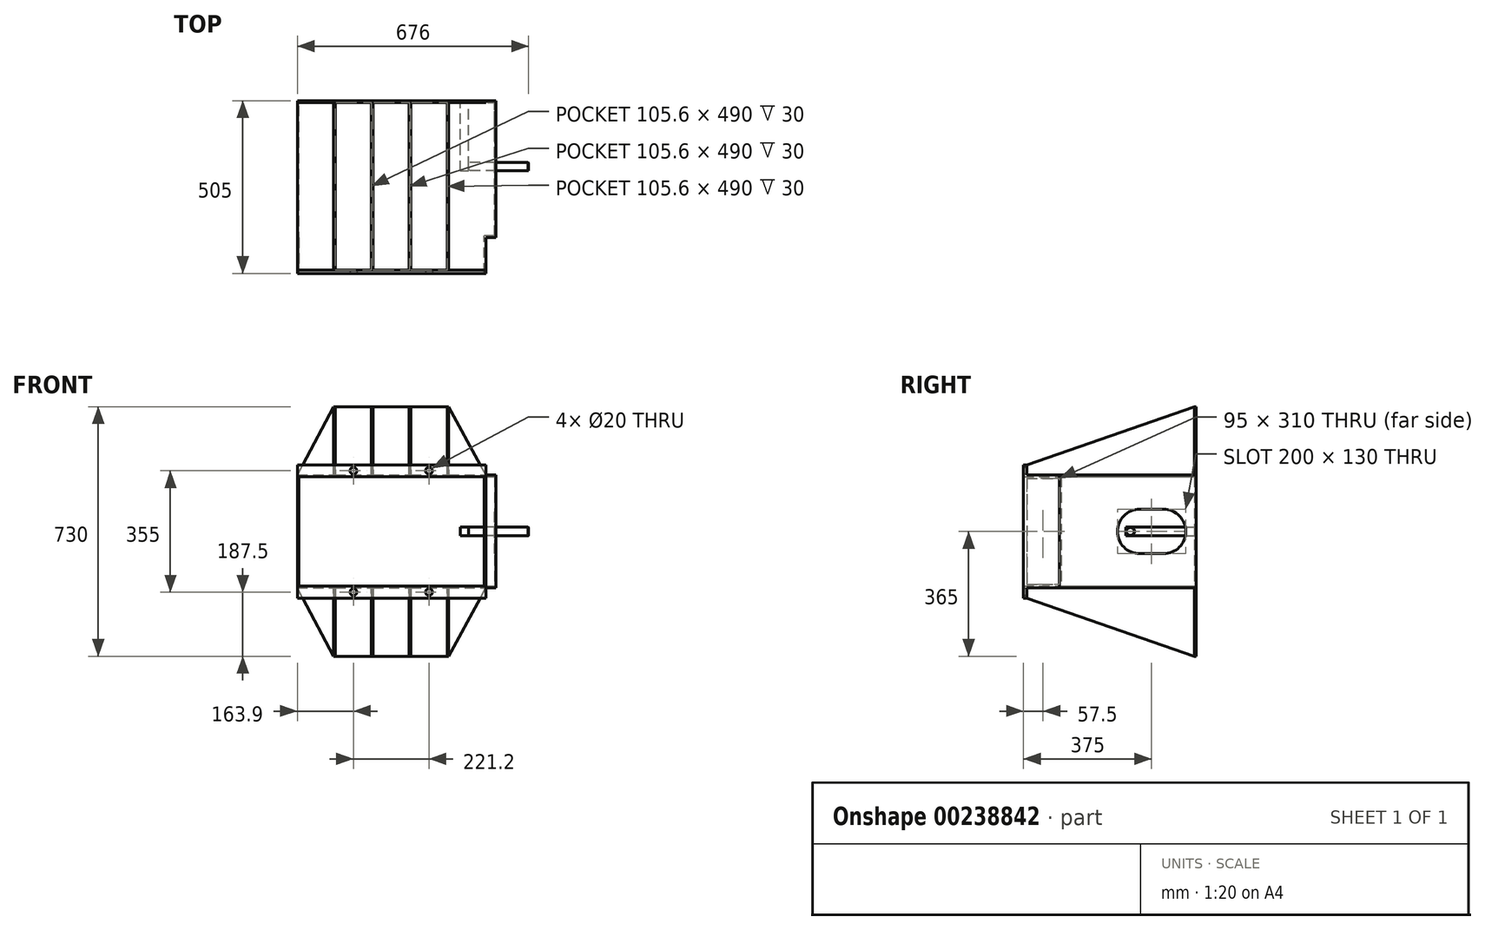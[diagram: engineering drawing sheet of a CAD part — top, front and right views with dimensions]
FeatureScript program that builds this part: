
annotation { "Feature Type Name" : "Feature", "Feature Type Description" : "" }
export const myFeature = defineFeature(function(context is Context, id is Id, definition is map)
    precondition{}
    {
        {
            var Q0;
            Q0=qCreatedBy(makeId("Front.planeOp"),FACE);
            var sketch = newSketch(context, id + "F0", { "sketchPlane" : qUnion([Q0])});
            skLineSegment(sketch, "E0.bottom", {"start": v(-376.5, 365) * mm, "end": v(376.5, 365) * mm});
            skLineSegment(sketch, "E0.top", {"start": v(-376.5, -365) * mm, "end": v(376.5, -365) * mm});
            skLineSegment(sketch, "E0.left", {"start": v(-376.5, 365) * mm, "end": v(-376.5, -365) * mm});
            skLineSegment(sketch, "E0.right", {"start": v(376.5, 365) * mm, "end": v(376.5, -365) * mm});
            skSolve(sketch);
        }
        {
            var Q0;
            Q0=makeQuery(id+"F0.imprint","IMPRINT",FACE,{"disambiguationData":[TD([[makeQuery(id+"F0.imprint","IMPRINT",EDGE,{"derivedFrom":sQuery(id+"F0.wireOp",EDGE,"E0.bottom")}),-1.0]])]});
            extrude(context, id + "F1", {"entities" : qUnion([Q0]), "depth" : 5 * mm});
        }
        {
            var Q0;
            Q0=makeQuery(id+"F1.opExtrude","CAP_FACE",FACE,{"disambiguationData":[OSD([sQuery(id+"F0.wireOp",EDGE,"E0.bottom"),sQuery(id+"F0.wireOp",EDGE,"E0.top"),sQuery(id+"F0.wireOp",EDGE,"E0.left"),sQuery(id+"F0.wireOp",EDGE,"E0.right")])],"isStart":false});
            var sketch = newSketch(context, id + "F2", { "sketchPlane" : qUnion([Q0])});
            skLineSegment(sketch, "E1.bottom", {"start": v(-276, 165) * mm, "end": v(275, 165) * mm});
            skLineSegment(sketch, "E1.top", {"start": v(-276, -165) * mm, "end": v(275, -165) * mm});
            skLineSegment(sketch, "E1.left", {"start": v(-276, 165) * mm, "end": v(-276, -165) * mm});
            skLineSegment(sketch, "E1.right", {"start": v(275, 165) * mm, "end": v(275, -165) * mm});
            skLineSegment(sketch, "E2.bottom", {"start": v(-272, 160) * mm, "end": v(271, 160) * mm});
            skLineSegment(sketch, "E2.top", {"start": v(-272, -160) * mm, "end": v(271, -160) * mm});
            skLineSegment(sketch, "E2.left", {"start": v(-272, 160) * mm, "end": v(-272, -160) * mm});
            skLineSegment(sketch, "E2.right", {"start": v(271, 160) * mm, "end": v(271, -160) * mm});
            skSolve(sketch);
        }
        {
            var Q0;
            Q0=makeQuery(id+"F2.imprint","IMPRINT",FACE,{"disambiguationData":[TD([[makeQuery(id+"F2.imprint","IMPRINT",EDGE,{"derivedFrom":sQuery(id+"F2.wireOp",EDGE,"E1.bottom")}),-1.0]])]});
            extrude(context, id + "F3", {"entities" : qUnion([Q0]), "operationType" : NewBodyOperationType.ADD, "depth" : 500 * mm});
        }
        {
            var Q0;
            Q0=makeQuery(id+"F3.opExtrude","SWEPT_FACE",FACE,{"disambiguationData":[OSD([sQuery(id+"F2.wireOp",EDGE,"E1.left")])]});
            var sketch = newSketch(context, id + "F4", { "sketchPlane" : qUnion([Q0])});
            skLineSegment(sketch, "E3.bottom", {"start": v(505, 165) * mm, "end": v(495, 165) * mm});
            skLineSegment(sketch, "E3.top", {"start": v(505, 195) * mm, "end": v(495, 195) * mm});
            skLineSegment(sketch, "E3.left", {"start": v(505, 165) * mm, "end": v(505, 195) * mm});
            skLineSegment(sketch, "E3.right", {"start": v(495, 165) * mm, "end": v(495, 195) * mm});
            skLineSegment(sketch, "E4.bottom", {"start": v(505, -165) * mm, "end": v(495, -165) * mm});
            skLineSegment(sketch, "E4.top", {"start": v(505, -195) * mm, "end": v(495, -195) * mm});
            skLineSegment(sketch, "E4.left", {"start": v(505, -165) * mm, "end": v(505, -195) * mm});
            skLineSegment(sketch, "E4.right", {"start": v(495, -165) * mm, "end": v(495, -195) * mm});
            skSolve(sketch);
        }
        {
            var Q0;
            Q0=makeQuery(id+"F4.imprint","IMPRINT",FACE,{"disambiguationData":[TD([[makeQuery(id+"F4.imprint","IMPRINT",EDGE,{"derivedFrom":sQuery(id+"F4.wireOp",EDGE,"E3.bottom")}),-1.0]])]});
            var Q1;
            Q1=makeQuery(id+"F4.imprint","IMPRINT",FACE,{"disambiguationData":[TD([[makeQuery(id+"F4.imprint","IMPRINT",EDGE,{"derivedFrom":sQuery(id+"F4.wireOp",EDGE,"E4.bottom")}),1.0]])]});
            var Q2;
            Q2=makeQuery(id+"F3.opExtrude","SWEPT_FACE",FACE,{"disambiguationData":[OSD([sQuery(id+"F2.wireOp",EDGE,"E1.right")])]});
            extrude(context, id + "F5", {"entities" : qUnion([Q0, Q1]), "operationType" : NewBodyOperationType.ADD, "endBound" : BoundingType.UP_TO_SURFACE, "oppositeDirection" : true, "endBoundEntityFace" : qUnion([Q2]), "depth" : 25 * mm});
        }
        {
            var Q0;
            {var subQ0=sQuery(id+"F0.wireOp",EDGE,"E0.right");var subQ1=sQuery(id+"F0.wireOp",EDGE,"E0.left");var subQ2=sQuery(id+"F0.wireOp",EDGE,"E0.top");var subQ3=sQuery(id+"F0.wireOp",EDGE,"E0.bottom");Q0=makeQuery(id+"F3.boolean.opBoolean","SPLIT",FACE,{"disambiguationData":[TD([makeQuery(id+"F1.opExtrude","SWEPT_FACE",FACE,{"disambiguationData":[OSD([subQ3])]})])],"derivedFrom":makeQuery(id+"F1.opExtrude","CAP_FACE",FACE,{"disambiguationData":[OSD([subQ3,subQ2,subQ1,subQ0])],"isStart":false})});}
            var sketch = newSketch(context, id + "F6", { "sketchPlane" : qUnion([Q0])});
            skLineSegment(sketch, "E5.bottom", {"start": v(166.9, 365) * mm, "end": v(161.9, 365) * mm});
            skLineSegment(sketch, "E5.top", {"start": v(166.9, 165) * mm, "end": v(161.9, 165) * mm});
            skLineSegment(sketch, "E5.left", {"start": v(166.9, 365) * mm, "end": v(166.9, 165) * mm});
            skLineSegment(sketch, "E5.right", {"start": v(161.9, 365) * mm, "end": v(161.9, 165) * mm});
            skLineSegment(sketch, "E6.bottom", {"start": v(56.3, 365) * mm, "end": v(51.3, 365) * mm});
            skLineSegment(sketch, "E6.top", {"start": v(56.3, 165) * mm, "end": v(51.3, 165) * mm});
            skLineSegment(sketch, "E6.left", {"start": v(56.3, 365) * mm, "end": v(56.3, 165) * mm});
            skLineSegment(sketch, "E6.right", {"start": v(51.3, 365) * mm, "end": v(51.3, 165) * mm});
            skLineSegment(sketch, "E7.bottom", {"start": v(-54.3, 365) * mm, "end": v(-59.3, 365) * mm});
            skLineSegment(sketch, "E7.top", {"start": v(-54.3, 165) * mm, "end": v(-59.3, 165) * mm});
            skLineSegment(sketch, "E7.left", {"start": v(-59.3, 365) * mm, "end": v(-59.3, 165) * mm});
            skLineSegment(sketch, "E7.right", {"start": v(-54.3, 365) * mm, "end": v(-54.3, 165) * mm});
            skLineSegment(sketch, "E8.bottom", {"start": v(-164.9, 365) * mm, "end": v(-169.9, 365) * mm});
            skLineSegment(sketch, "E8.top", {"start": v(-164.9, 165) * mm, "end": v(-169.9, 165) * mm});
            skLineSegment(sketch, "E8.left", {"start": v(-169.9, 365) * mm, "end": v(-169.9, 165) * mm});
            skLineSegment(sketch, "E8.right", {"start": v(-164.9, 365) * mm, "end": v(-164.9, 165) * mm});
            skPoint(sketch, "E9.oppositeSnap0", {"position": v(161.9, 265) * mm});
            skLineSegment(sketch, "E9.bottom", {"start": v(166.9, -365) * mm, "end": v(161.9, -365) * mm});
            skLineSegment(sketch, "E9.top", {"start": v(166.9, -165) * mm, "end": v(161.9, -165) * mm});
            skLineSegment(sketch, "E9.left", {"start": v(166.9, -365) * mm, "end": v(166.9, -165) * mm});
            skLineSegment(sketch, "E9.right", {"start": v(161.9, -365) * mm, "end": v(161.9, -165) * mm});
            skPoint(sketch, "E10.firstSnap0", {"position": v(56.3, 265) * mm});
            skLineSegment(sketch, "E10.bottom", {"start": v(56.3, -365) * mm, "end": v(51.3, -365) * mm});
            skLineSegment(sketch, "E10.top", {"start": v(56.3, -165) * mm, "end": v(51.3, -165) * mm});
            skLineSegment(sketch, "E10.left", {"start": v(56.3, -365) * mm, "end": v(56.3, -165) * mm});
            skLineSegment(sketch, "E10.right", {"start": v(51.3, -365) * mm, "end": v(51.3, -165) * mm});
            skLineSegment(sketch, "E11.bottom", {"start": v(-54.3, -365) * mm, "end": v(-59.3, -365) * mm});
            skLineSegment(sketch, "E11.top", {"start": v(-54.3, -165) * mm, "end": v(-59.3, -165) * mm});
            skLineSegment(sketch, "E11.left", {"start": v(-54.3, -365) * mm, "end": v(-54.3, -165) * mm});
            skLineSegment(sketch, "E11.right", {"start": v(-59.3, -365) * mm, "end": v(-59.3, -165) * mm});
            skPoint(sketch, "E12.oppositeSnap0", {"position": v(-169.9, 265) * mm});
            skLineSegment(sketch, "E12.bottom", {"start": v(-164.9, -365) * mm, "end": v(-169.9, -365) * mm});
            skLineSegment(sketch, "E12.top", {"start": v(-164.9, -165) * mm, "end": v(-169.9, -165) * mm});
            skLineSegment(sketch, "E12.left", {"start": v(-164.9, -365) * mm, "end": v(-164.9, -165) * mm});
            skLineSegment(sketch, "E12.right", {"start": v(-169.9, -365) * mm, "end": v(-169.9, -165) * mm});
            skSolve(sketch);
        }
        {
            var Q0;
            Q0 = qSketchRegion(id + "F6", true);
            var Q1;
            Q1=makeQuery(id+"F5.opExtrude","SWEPT_FACE",FACE,{"disambiguationData":[OSD([sQuery(id+"F4.wireOp",EDGE,"E4.right")])]});
            extrude(context, id + "F7", {"entities" : qUnion([Q0]), "operationType" : NewBodyOperationType.ADD, "endBound" : BoundingType.UP_TO_SURFACE, "endBoundEntityFace" : qUnion([Q1]), "depth" : 25 * mm});
        }
        {
            var Q0;
            Q0=makeQuery(id+"F7.opExtrude","SWEPT_FACE",FACE,{"disambiguationData":[OSD([sQuery(id+"F6.wireOp",EDGE,"E8.left")])]});
            var sketch = newSketch(context, id + "F8", { "sketchPlane" : qUnion([Q0])});
            skLineSegment(sketch, "E13", {"start": v(495, 195) * mm, "end": v(5, 365) * mm});
            skLineSegment(sketch, "E14", {"start": v(5, 365) * mm, "end": v(495, 365) * mm});
            skLineSegment(sketch, "E15", {"start": v(495, 365) * mm, "end": v(495, 195) * mm});
            skSolve(sketch);
        }
        {
            var Q0;
            Q0=makeQuery(id+"F7.opExtrude","SWEPT_FACE",FACE,{"disambiguationData":[OSD([sQuery(id+"F6.wireOp",EDGE,"E12.right")])]});
            var sketch = newSketch(context, id + "F9", { "sketchPlane" : qUnion([Q0])});
            skLineSegment(sketch, "E16", {"start": v(495, -195) * mm, "end": v(5, -365) * mm});
            skLineSegment(sketch, "E17", {"start": v(495, -195) * mm, "end": v(495, -365) * mm});
            skLineSegment(sketch, "E18", {"start": v(495, -365) * mm, "end": v(5, -365) * mm});
            skSolve(sketch);
        }
        {
            var Q0;
            Q0=makeQuery(id+"F8.imprint","IMPRINT",FACE,{"disambiguationData":[TD([[makeQuery(id+"F8.imprint","IMPRINT",EDGE,{"derivedFrom":sQuery(id+"F8.wireOp",EDGE,"E13")}),-1.0]])]});
            var Q1;
            Q1=makeQuery(id+"F9.imprint","IMPRINT",FACE,{"disambiguationData":[TD([[makeQuery(id+"F9.imprint","IMPRINT",EDGE,{"derivedFrom":sQuery(id+"F9.wireOp",EDGE,"E16")}),1.0]])]});
            extrude(context, id + "F10", {"entities" : qUnion([Q0, Q1]), "operationType" : NewBodyOperationType.REMOVE, "endBound" : BoundingType.THROUGH_ALL, "oppositeDirection" : true, "depth" : 25 * mm});
        }
        {
            var Q0;
            {var subQ1=sQuery(id+"F0.wireOp",EDGE,"E0.right");var subQ2=makeQuery(id+"F1.opExtrude","SWEPT_FACE",FACE,{"disambiguationData":[OSD([subQ1])]});var subQ5=sQuery(id+"F0.wireOp",EDGE,"E0.bottom");var subQ6=makeQuery(id+"F1.opExtrude","SWEPT_FACE",FACE,{"disambiguationData":[OSD([subQ5])]});var subQ8=sQuery(id+"F0.wireOp",EDGE,"E0.top");var subQ10=sQuery(id+"F0.wireOp",EDGE,"E0.left");Q0=makeQuery(id+"F7.boolean.opBoolean","SPLIT",FACE,{"disambiguationData":[TD([subQ2])],"derivedFrom":makeQuery(id+"F3.boolean.opBoolean","SPLIT",FACE,{"disambiguationData":[TD([subQ6])],"derivedFrom":makeQuery(id+"F1.opExtrude","CAP_FACE",FACE,{"disambiguationData":[OSD([subQ5,subQ8,subQ10,subQ1])],"isStart":false})})});}
            var sketch = newSketch(context, id + "F11", { "sketchPlane" : qUnion([Q0])});
            skLineSegment(sketch, "E19", {"start": v(166.9, -365) * mm, "end": v(275, -165) * mm});
            skLineSegment(sketch, "E20", {"start": v(275, -165) * mm, "end": v(275, 165) * mm});
            skLineSegment(sketch, "E21", {"start": v(275, 165) * mm, "end": v(166.9, 365) * mm});
            skLineSegment(sketch, "E22", {"start": v(166.9, 365) * mm, "end": v(376.5, 365) * mm});
            skLineSegment(sketch, "E23", {"start": v(376.5, 365) * mm, "end": v(376.5, -365) * mm});
            skLineSegment(sketch, "E24", {"start": v(376.5, -365) * mm, "end": v(166.9, -365) * mm});
            skSolve(sketch);
        }
        {
            var Q0;
            {var subQ1=sQuery(id+"F0.wireOp",EDGE,"E0.left");var subQ2=makeQuery(id+"F1.opExtrude","SWEPT_FACE",FACE,{"disambiguationData":[OSD([subQ1])]});var subQ4=sQuery(id+"F0.wireOp",EDGE,"E0.bottom");var subQ5=makeQuery(id+"F1.opExtrude","SWEPT_FACE",FACE,{"disambiguationData":[OSD([subQ4])]});var subQ7=sQuery(id+"F0.wireOp",EDGE,"E0.top");var subQ9=sQuery(id+"F0.wireOp",EDGE,"E0.right");Q0=makeQuery(id+"F7.boolean.opBoolean","SPLIT",FACE,{"disambiguationData":[TD([subQ2])],"derivedFrom":makeQuery(id+"F3.boolean.opBoolean","SPLIT",FACE,{"disambiguationData":[TD([subQ5])],"derivedFrom":makeQuery(id+"F1.opExtrude","CAP_FACE",FACE,{"disambiguationData":[OSD([subQ4,subQ7,subQ1,subQ9])],"isStart":false})})});}
            var sketch = newSketch(context, id + "F12", { "sketchPlane" : qUnion([Q0])});
            skLineSegment(sketch, "E25", {"start": v(-169.9, -365) * mm, "end": v(-276, -165) * mm});
            skLineSegment(sketch, "E26", {"start": v(-276, -165) * mm, "end": v(-276, 165) * mm});
            skLineSegment(sketch, "E27", {"start": v(-276, 165) * mm, "end": v(-169.9, 365) * mm});
            skLineSegment(sketch, "E28", {"start": v(-169.9, 365) * mm, "end": v(-376.5, 365) * mm});
            skLineSegment(sketch, "E29", {"start": v(-376.5, 365) * mm, "end": v(-376.5, -365) * mm});
            skLineSegment(sketch, "E30", {"start": v(-376.5, -365) * mm, "end": v(-169.9, -365) * mm});
            skSolve(sketch);
        }
        {
            var Q0;
            Q0=makeQuery(id+"F11.imprint","IMPRINT",FACE,{"disambiguationData":[TD([[makeQuery(id+"F11.imprint","IMPRINT",EDGE,{"derivedFrom":sQuery(id+"F11.wireOp",EDGE,"E19")}),-1.0]])]});
            var Q1;
            Q1=makeQuery(id+"F12.imprint","IMPRINT",FACE,{"disambiguationData":[TD([[makeQuery(id+"F12.imprint","IMPRINT",EDGE,{"derivedFrom":sQuery(id+"F12.wireOp",EDGE,"E25")}),1.0]])]});
            extrude(context, id + "F13", {"entities" : qUnion([Q0, Q1]), "operationType" : NewBodyOperationType.REMOVE, "endBound" : BoundingType.THROUGH_ALL, "oppositeDirection" : true, "depth" : 25 * mm});
        }
        {
            var Q0;
            {var subQ0=sQuery(id+"F2.wireOp",EDGE,"E1.right");Q0=makeQuery(id+"F13.boolean.opBoolean","MERGE",FACE,{"derivedFrom":[makeQuery(id+"F5.boolean.opBoolean","MERGE",FACE,{"derivedFrom":[makeQuery(id+"F3.opExtrude","SWEPT_FACE",FACE,{"disambiguationData":[OSD([subQ0])]}),makeQuery(id+"F5.opExtrude","CAP_FACE",FACE,{"disambiguationData":[OSD([subQ0]),ownerDisambiguation([makeQuery(id+"F5.opExtrude","SWEPT_BODY",BODY,{"disambiguationData":[OSD([sQuery(id+"F4.wireOp",EDGE,"E3.bottom"),sQuery(id+"F4.wireOp",EDGE,"E3.top"),sQuery(id+"F4.wireOp",EDGE,"E3.left"),sQuery(id+"F4.wireOp",EDGE,"E3.right")])]})])],"isStart":false}),makeQuery(id+"F5.opExtrude","CAP_FACE",FACE,{"disambiguationData":[OSD([subQ0]),ownerDisambiguation([makeQuery(id+"F5.opExtrude","SWEPT_BODY",BODY,{"disambiguationData":[OSD([sQuery(id+"F4.wireOp",EDGE,"E4.bottom"),sQuery(id+"F4.wireOp",EDGE,"E4.top"),sQuery(id+"F4.wireOp",EDGE,"E4.left"),sQuery(id+"F4.wireOp",EDGE,"E4.right")])]})])],"isStart":false})]}),makeQuery(id+"F13.opExtrude","SWEPT_FACE",FACE,{"disambiguationData":[OSD([sQuery(id+"F11.wireOp",EDGE,"E20")])]})]});}
            var sketch = newSketch(context, id + "F14", { "sketchPlane" : qUnion([Q0])});
            skLineSegment(sketch, "E31.bottom", {"start": v(0, -165) * mm, "end": v(-400, -165) * mm});
            skLineSegment(sketch, "E31.top", {"start": v(0, 165) * mm, "end": v(-400, 165) * mm});
            skLineSegment(sketch, "E31.left", {"start": v(0, -165) * mm, "end": v(0, 165) * mm});
            skLineSegment(sketch, "E31.right", {"start": v(-400, -165) * mm, "end": v(-400, 165) * mm});
            skSolve(sketch);
        }
        {
            var Q0;
            {var subQ2=sQuery(id+"F14.wireOp",EDGE,"E31.left");Q0=makeQuery(id+"F14.imprint","IMPRINT",FACE,{"disambiguationData":[TD([[makeQuery(id+"F14.imprint","IMPRINT",EDGE,{"derivedFrom":subQ2}),-1.0]])]});}
            extrude(context, id + "F15", {"entities" : qUnion([Q0]), "operationType" : NewBodyOperationType.ADD, "depth" : 30 * mm});
        }
        {
            var Q0;
            Q0=makeQuery(id+"F3.opExtrude","SWEPT_FACE",FACE,{"disambiguationData":[OSD([sQuery(id+"F2.wireOp",EDGE,"E2.right")])]});
            var sketch = newSketch(context, id + "F16", { "sketchPlane" : qUnion([Q0])});
            skLineSegment(sketch, "E32.bottom", {"start": v(5, 160) * mm, "end": v(395, 160) * mm});
            skLineSegment(sketch, "E32.top", {"start": v(5, -160) * mm, "end": v(395, -160) * mm});
            skLineSegment(sketch, "E32.left", {"start": v(5, 160) * mm, "end": v(5, -160) * mm});
            skLineSegment(sketch, "E32.right", {"start": v(395, 160) * mm, "end": v(395, -160) * mm});
            skSolve(sketch);
        }
        {
            var Q0;
            Q0=makeQuery(id+"F16.imprint","IMPRINT",FACE,{"disambiguationData":[TD([[makeQuery(id+"F16.imprint","IMPRINT",EDGE,{"derivedFrom":sQuery(id+"F16.wireOp",EDGE,"E32.bottom")}),1.0]])]});
            extrude(context, id + "F17", {"entities" : qUnion([Q0]), "operationType" : NewBodyOperationType.REMOVE, "oppositeDirection" : true, "depth" : 30 * mm});
        }
        {
            var Q0;
            Q0=makeQuery(id+"F15.opExtrude","CAP_FACE",FACE,{"disambiguationData":[OSD([sQuery(id+"F14.wireOp",EDGE,"E31.bottom"),sQuery(id+"F14.wireOp",EDGE,"E31.top"),sQuery(id+"F14.wireOp",EDGE,"E31.left"),sQuery(id+"F14.wireOp",EDGE,"E31.right")])],"isStart":false});
            var sketch = newSketch(context, id + "F18", { "sketchPlane" : qUnion([Q0])});
            skLineSegment(sketch, "E33.bottom", {"start": v(-165, -65) * mm, "end": v(-95, -65) * mm});
            skLineSegment(sketch, "E33.top", {"start": v(-165, 65) * mm, "end": v(-95, 65) * mm});
            skLineSegment(sketch, "E33.left", {"start": v(-165, -65) * mm, "end": v(-165, 65) * mm});
            skLineSegment(sketch, "E33.right", {"start": v(-95, -65) * mm, "end": v(-95, 65) * mm});
            skArc(sketch, "E34", {"start": v(-165, 65) * mm, "mid": v(-230, 0) * mm, "end": v(-165, -65) * mm});
            skArc(sketch, "E35", {"start": v(-95, -65) * mm, "mid": v(-30, 0) * mm, "end": v(-95, 65) * mm});
            skLineSegment(sketch, "E36", {"start": v(-165, 0) * mm, "end": v(-95, 0) * mm, "construction": true});
            skSolve(sketch);
        }
        {
            var Q0;
            Q0=makeQuery(id+"F18.imprint","IMPRINT",FACE,{"disambiguationData":[TD([[makeQuery(id+"F18.imprint","IMPRINT",EDGE,{"derivedFrom":sQuery(id+"F18.wireOp",EDGE,"E33.left")}),1.0]])]});
            var Q1;
            Q1=makeQuery(id+"F18.imprint","IMPRINT",FACE,{"disambiguationData":[TD([[makeQuery(id+"F18.imprint","IMPRINT",EDGE,{"derivedFrom":sQuery(id+"F18.wireOp",EDGE,"E33.bottom")}),1.0]])]});
            var Q2;
            Q2=makeQuery(id+"F18.imprint","IMPRINT",FACE,{"disambiguationData":[TD([[makeQuery(id+"F18.imprint","IMPRINT",EDGE,{"derivedFrom":sQuery(id+"F18.wireOp",EDGE,"E33.right")}),-1.0]])]});
            extrude(context, id + "F19", {"entities" : qUnion([Q0, Q1, Q2]), "operationType" : NewBodyOperationType.REMOVE, "oppositeDirection" : true, "depth" : 5 * mm});
        }
        {
            var Q0;
            Q0=makeQuery(id+"F13.boolean.opBoolean","MERGE",FACE,{"derivedFrom":[makeQuery(id+"F5.boolean.opBoolean","MERGE",FACE,{"derivedFrom":[makeQuery(id+"F3.opExtrude","SWEPT_FACE",FACE,{"disambiguationData":[OSD([sQuery(id+"F2.wireOp",EDGE,"E1.left")])]}),makeQuery(id+"F5.opExtrude","CAP_FACE",FACE,{"disambiguationData":[OSD([sQuery(id+"F4.wireOp",EDGE,"E3.bottom"),sQuery(id+"F4.wireOp",EDGE,"E3.top"),sQuery(id+"F4.wireOp",EDGE,"E3.left"),sQuery(id+"F4.wireOp",EDGE,"E3.right")])],"isStart":true}),makeQuery(id+"F5.opExtrude","CAP_FACE",FACE,{"disambiguationData":[OSD([sQuery(id+"F4.wireOp",EDGE,"E4.bottom"),sQuery(id+"F4.wireOp",EDGE,"E4.top"),sQuery(id+"F4.wireOp",EDGE,"E4.left"),sQuery(id+"F4.wireOp",EDGE,"E4.right")])],"isStart":true})]}),makeQuery(id+"F13.opExtrude","SWEPT_FACE",FACE,{"disambiguationData":[OSD([sQuery(id+"F12.wireOp",EDGE,"E26")])]})]});
            var sketch = newSketch(context, id + "F20", { "sketchPlane" : qUnion([Q0])});
            skLineSegment(sketch, "E37.bottom", {"start": v(495, 155) * mm, "end": v(400, 155) * mm});
            skLineSegment(sketch, "E37.top", {"start": v(495, -155) * mm, "end": v(400, -155) * mm});
            skLineSegment(sketch, "E37.left", {"start": v(495, 155) * mm, "end": v(495, -155) * mm});
            skLineSegment(sketch, "E37.right", {"start": v(400, 155) * mm, "end": v(400, -155) * mm});
            skSolve(sketch);
        }
        {
            var Q0;
            Q0=makeQuery(id+"F20.imprint","IMPRINT",FACE,{"disambiguationData":[TD([[makeQuery(id+"F20.imprint","IMPRINT",EDGE,{"derivedFrom":sQuery(id+"F20.wireOp",EDGE,"E37.bottom")}),1.0]])]});
            extrude(context, id + "F21", {"entities" : qUnion([Q0]), "operationType" : NewBodyOperationType.REMOVE, "oppositeDirection" : true, "depth" : 5 * mm});
        }
        {
            var Q0;
            Q0=makeQuery(id+"F17.boolean.opBoolean","MERGE",FACE,{"derivedFrom":[makeQuery(id+"F3.boolean.opBoolean","SPLIT",FACE,{"disambiguationData":[TD([makeQuery(id+"F3.opExtrude","SWEPT_FACE",FACE,{"disambiguationData":[OSD([sQuery(id+"F2.wireOp",EDGE,"E2.bottom")])]})])],"derivedFrom":makeQuery(id+"F1.opExtrude","CAP_FACE",FACE,{"disambiguationData":[OSD([sQuery(id+"F0.wireOp",EDGE,"E0.bottom"),sQuery(id+"F0.wireOp",EDGE,"E0.top"),sQuery(id+"F0.wireOp",EDGE,"E0.left"),sQuery(id+"F0.wireOp",EDGE,"E0.right")])],"isStart":false})}),makeQuery(id+"F17.opExtrude","SWEPT_FACE",FACE,{"disambiguationData":[OSD([sQuery(id+"F16.wireOp",EDGE,"E32.left")])]})]});
            var sketch = newSketch(context, id + "F22", { "sketchPlane" : qUnion([Q0])});
            skLineSegment(sketch, "E38.bottom", {"start": v(200, 12.5) * mm, "end": v(225, 12.5) * mm});
            skLineSegment(sketch, "E38.top", {"start": v(200, -12.5) * mm, "end": v(225, -12.5) * mm});
            skLineSegment(sketch, "E38.left", {"start": v(200, 12.5) * mm, "end": v(200, -12.5) * mm});
            skLineSegment(sketch, "E38.right", {"start": v(225, 12.5) * mm, "end": v(225, -12.5) * mm});
            skSolve(sketch);
        }
        {
            var Q0;
            Q0=makeQuery(id+"F22.imprint","IMPRINT",FACE,{"disambiguationData":[TD([[makeQuery(id+"F22.imprint","IMPRINT",EDGE,{"derivedFrom":sQuery(id+"F22.wireOp",EDGE,"E38.bottom")}),-1.0]])]});
            extrude(context, id + "F23", {"entities" : qUnion([Q0]), "operationType" : NewBodyOperationType.ADD, "depth" : 200 * mm});
        }
        {
            var Q0;
            Q0=makeQuery(id+"F23.opExtrude","SWEPT_FACE",FACE,{"disambiguationData":[OSD([sQuery(id+"F22.wireOp",EDGE,"E38.right")])]});
            var sketch = newSketch(context, id + "F24", { "sketchPlane" : qUnion([Q0])});
            skCircle(sketch, "E39", {"center": v(-192.5, 0) * mm, "radius": 12.5 * mm});
            skSolve(sketch);
        }
        {
            var Q0;
            {var subQ0=sQuery(id+"F24.wireOp",EDGE,"E39");var subQ1=sQuery(id+"F22.wireOp",EDGE,"E38.right");var subQ2=makeQuery(id+"F24.imprint","INTERSECT",VERTEX,{"derivedFrom":[makeQuery(id+"F23.opExtrude","CAP_EDGE",EDGE,{"disambiguationData":[OSD([subQ1])],"isStart":false}),subQ0]});Q0=makeQuery(id+"F24.imprint","IMPRINT",FACE,{"disambiguationData":[TD([[makeQuery(id+"F24.imprint","IMPRINT",EDGE,{"disambiguationData":[TD([[subQ2,1.0]])],"derivedFrom":subQ0}),1.0]])]});}
            extrude(context, id + "F25", {"entities" : qUnion([Q0]), "operationType" : NewBodyOperationType.ADD, "depth" : 175 * mm});
        }
        {
            var Q0;
            Q0=makeQuery(id+"F25.opExtrude","CAP_EDGE",EDGE,{"disambiguationData":[OSD([sQuery(id+"F24.wireOp",EDGE,"E39")])],"isStart":false});
            chamfer(context, id + "F26", {"entities" : qUnion([Q0]), "width" : 1.1 * mm, "tangentPropagation" : true});
        }
        {
            var Q0;
            Q0=makeQuery(id+"F5.boolean.opBoolean","MERGE",FACE,{"derivedFrom":[makeQuery(id+"F3.opExtrude","CAP_FACE",FACE,{"disambiguationData":[OSD([sQuery(id+"F2.wireOp",EDGE,"E1.bottom"),sQuery(id+"F2.wireOp",EDGE,"E1.top"),sQuery(id+"F2.wireOp",EDGE,"E1.left"),sQuery(id+"F2.wireOp",EDGE,"E1.right"),sQuery(id+"F2.wireOp",EDGE,"E2.bottom"),sQuery(id+"F2.wireOp",EDGE,"E2.top"),sQuery(id+"F2.wireOp",EDGE,"E2.left"),sQuery(id+"F2.wireOp",EDGE,"E2.right")])],"isStart":false}),makeQuery(id+"F5.opExtrude","SWEPT_FACE",FACE,{"disambiguationData":[OSD([sQuery(id+"F4.wireOp",EDGE,"E3.left")])]}),makeQuery(id+"F5.opExtrude","SWEPT_FACE",FACE,{"disambiguationData":[OSD([sQuery(id+"F4.wireOp",EDGE,"E4.left")])]})]});
            var sketch = newSketch(context, id + "F27", { "sketchPlane" : qUnion([Q0])});
            skCircle(sketch, "E40", {"center": v(109.1, 177.5) * mm, "radius": 10 * mm});
            skCircle(sketch, "E41", {"center": v(-112.1, 177.5) * mm, "radius": 10 * mm});
            skCircle(sketch, "E42", {"center": v(109.1, -177.5) * mm, "radius": 10 * mm});
            skCircle(sketch, "E43", {"center": v(-112.1, -177.5) * mm, "radius": 10 * mm});
            skSolve(sketch);
        }
        {
            var Q0;
            Q0=makeQuery(id+"F27.imprint","IMPRINT",FACE,{"disambiguationData":[TD([[makeQuery(id+"F27.imprint","IMPRINT",EDGE,{"derivedFrom":sQuery(id+"F27.wireOp",EDGE,"E40")}),1.0]])]});
            var Q1;
            Q1=makeQuery(id+"F27.imprint","IMPRINT",FACE,{"disambiguationData":[TD([[makeQuery(id+"F27.imprint","IMPRINT",EDGE,{"derivedFrom":sQuery(id+"F27.wireOp",EDGE,"E41")}),1.0]])]});
            var Q2;
            Q2=makeQuery(id+"F27.imprint","IMPRINT",FACE,{"disambiguationData":[TD([[makeQuery(id+"F27.imprint","IMPRINT",EDGE,{"derivedFrom":sQuery(id+"F27.wireOp",EDGE,"E43")}),1.0]])]});
            var Q3;
            Q3=makeQuery(id+"F27.imprint","IMPRINT",FACE,{"disambiguationData":[TD([[makeQuery(id+"F27.imprint","IMPRINT",EDGE,{"derivedFrom":sQuery(id+"F27.wireOp",EDGE,"E42")}),1.0]])]});
            extrude(context, id + "F28", {"entities" : qUnion([Q0, Q1, Q2, Q3]), "operationType" : NewBodyOperationType.REMOVE, "oppositeDirection" : true, "depth" : 25 * mm});
        }
    });
